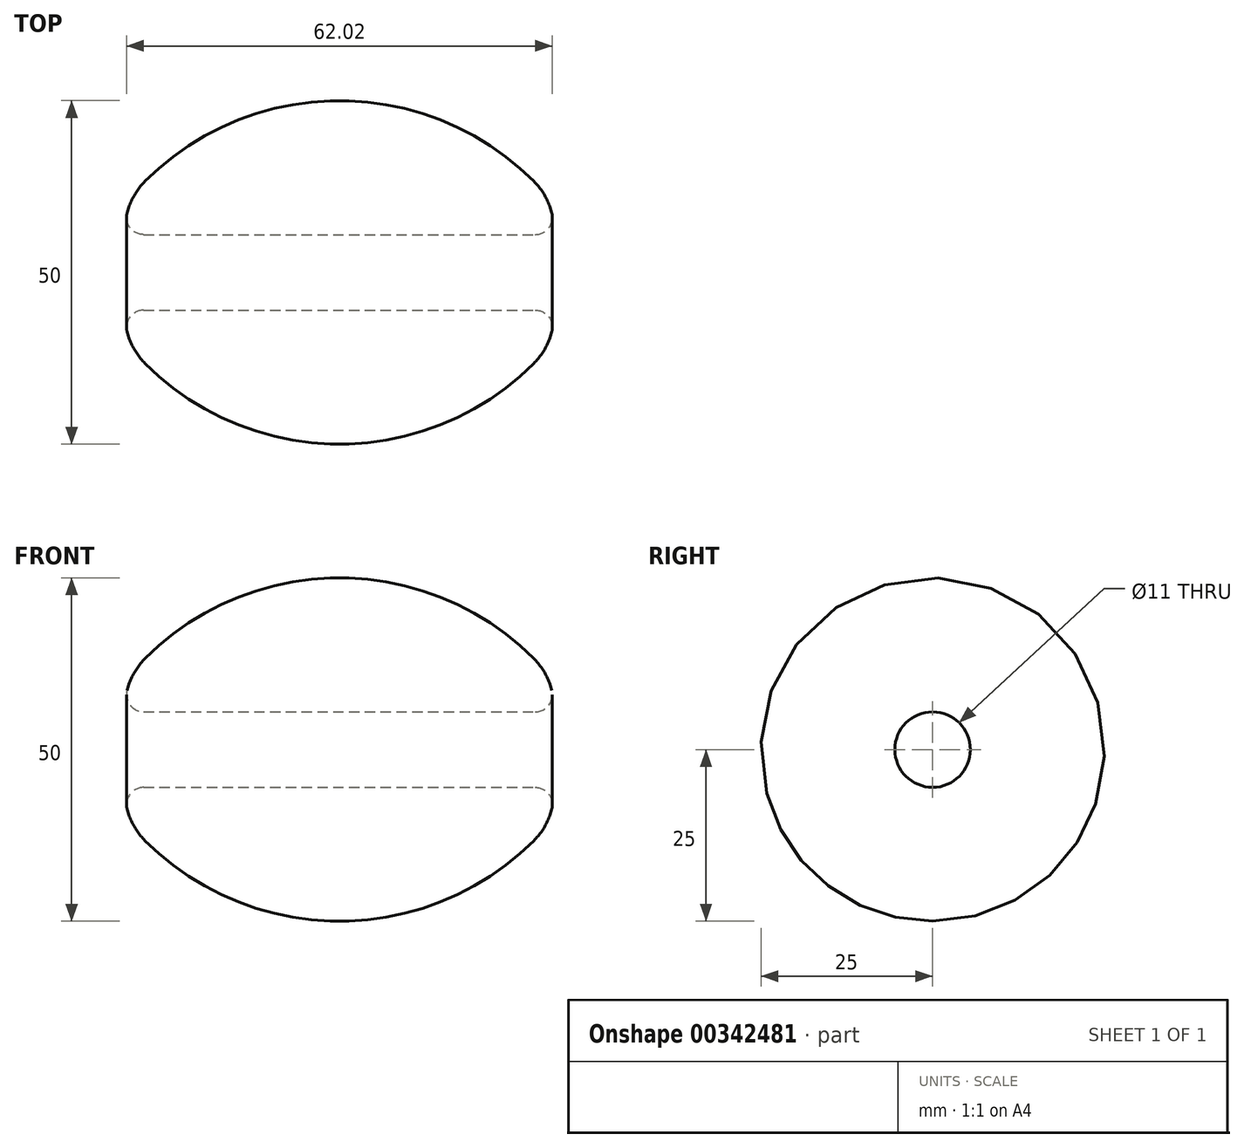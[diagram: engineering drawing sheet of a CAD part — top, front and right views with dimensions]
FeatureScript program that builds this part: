
annotation { "Feature Type Name" : "Feature", "Feature Type Description" : "" }
export const myFeature = defineFeature(function(context is Context, id is Id, definition is map)
    precondition{}
    {
        {
            var Q0;
            Q0=qCreatedBy(makeId("Front.planeOp"),FACE);
            var sketch = newSketch(context, id + "F0", { "sketchPlane" : qUnion([Q0])});
            skCircle(sketch, "E0", {"center": v(0, -15) * mm, "radius": 40 * mm});
            skLineSegment(sketch, "E1", {"start": v(-31.22, 10) * mm, "end": v(-31.22, 0) * mm});
            skLineSegment(sketch, "E2", {"start": v(-31.22, 0) * mm, "end": v(0, 0) * mm});
            skLineSegment(sketch, "E3", {"start": v(31.22, 10) * mm, "end": v(31.22, 0) * mm});
            skLineSegment(sketch, "E4", {"start": v(0, 0) * mm, "end": v(31.22, 0) * mm});
            skSolve(sketch);
        }
        {
            var Q0;
            {var subQ1=sQuery(id+"F0.wireOp",EDGE,"E1");Q0=makeQuery(id+"F0.imprint","IMPRINT",FACE,{"disambiguationData":[TD([[makeQuery(id+"F0.imprint","IMPRINT",EDGE,{"derivedFrom":subQ1}),1.0]])]});}
            var Q1;
            Q1=sQuery(id+"F0.wireOp",EDGE,"E2");
            revolve(context, id + "F1", {"entities" : qUnion([Q0]), "axis" : qUnion([Q1]), "revolveType" : RevolveType.FULL});
        }
        {
            var Q0;
            Q0=makeQuery(id+"F1.opRevolve","SWEPT_EDGE",EDGE,{"disambiguationData":[OSD([sQuery(id+"F0.wireOp",EDGE,"E0"),sQuery(id+"F0.wireOp",EDGE,"E1")])]});
            var Q1;
            Q1=makeQuery(id+"F1.opRevolve","SWEPT_EDGE",EDGE,{"disambiguationData":[OSD([sQuery(id+"F0.wireOp",EDGE,"E0"),sQuery(id+"F0.wireOp",EDGE,"E3")])]});
            fillet(context, id + "F2", {"entities" : qUnion([Q0, Q1]), "radius" : 10 * mm, "tangentPropagation" : true, "allowEdgeOverflow" : false});
        }
        {
            var Q0;
            Q0=qCreatedBy(makeId("Right.planeOp"),FACE);
            var sketch = newSketch(context, id + "F3", { "sketchPlane" : qUnion([Q0])});
            skCircle(sketch, "E5", {"center": v(0, 0) * mm, "radius": 5.5 * mm});
            skSolve(sketch);
        }
        {
            var Q0;
            Q0=makeQuery(id+"F3.imprint","IMPRINT",FACE,{"disambiguationData":[TD([[makeQuery(id+"F3.imprint","IMPRINT",EDGE,{"derivedFrom":sQuery(id+"F3.wireOp",EDGE,"E5")}),1.0]])]});
            extrude(context, id + "F4", {"entities" : qUnion([Q0]), "operationType" : NewBodyOperationType.REMOVE, "oppositeDirection" : true, "depth" : 200 * mm, "symmetric" : true});
        }
        {
            var Q0;
            Q0=makeQuery(id+"F4.boolean.opBoolean","INTERSECT",EDGE,{"derivedFrom":[makeQuery(id+"F1.opRevolve","SWEPT_FACE",FACE,{"disambiguationData":[OSD([sQuery(id+"F0.wireOp",EDGE,"E1")])]}),makeQuery(id+"F4.opExtrude","SWEPT_FACE",FACE,{"disambiguationData":[OSD([sQuery(id+"F3.wireOp",EDGE,"E5")])]})]});
            var Q1;
            Q1=makeQuery(id+"F4.boolean.opBoolean","INTERSECT",EDGE,{"derivedFrom":[makeQuery(id+"F1.opRevolve","SWEPT_FACE",FACE,{"disambiguationData":[OSD([sQuery(id+"F0.wireOp",EDGE,"E3")])]}),makeQuery(id+"F4.opExtrude","SWEPT_FACE",FACE,{"disambiguationData":[OSD([sQuery(id+"F3.wireOp",EDGE,"E5")])]})]});
            fillet(context, id + "F5", {"entities" : qUnion([Q0, Q1]), "radius" : 2.5 * mm, "tangentPropagation" : true, "allowEdgeOverflow" : false});
        }
    });
